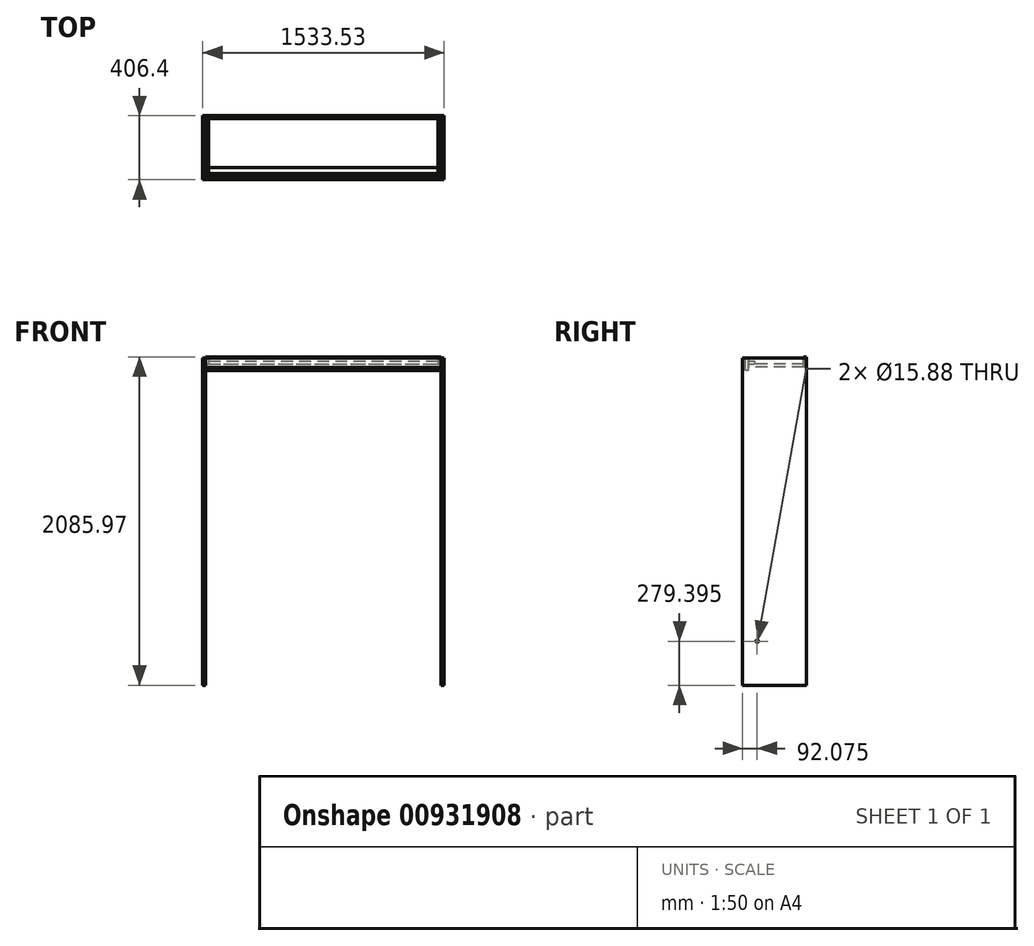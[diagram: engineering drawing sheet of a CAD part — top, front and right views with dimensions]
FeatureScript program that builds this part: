
annotation { "Feature Type Name" : "Feature", "Feature Type Description" : "" }
export const myFeature = defineFeature(function(context is Context, id is Id, definition is map)
    precondition{}
    {
        {
            var Q0;
            Q0=qCreatedBy(makeId("Top.planeOp"),FACE);
            var sketch = newSketch(context, id + "F0", { "sketchPlane" : qUnion([Q0])});
            skLineSegment(sketch, "E0.bottom", {"start": v(0, 0) * mm, "end": v(1495.43, 0) * mm});
            skLineSegment(sketch, "E0.top", {"start": v(0, -349.25) * mm, "end": v(1495.43, -349.25) * mm});
            skLineSegment(sketch, "E0.left", {"start": v(0, 0) * mm, "end": v(0, -349.25) * mm});
            skLineSegment(sketch, "E0.right", {"start": v(1495.43, 0) * mm, "end": v(1495.43, -349.25) * mm});
            skSolve(sketch);
        }
        {
            var Q0;
            Q0=makeQuery(id+"F0.imprint","IMPRINT",FACE,{"disambiguationData":[TD([[makeQuery(id+"F0.imprint","IMPRINT",EDGE,{"derivedFrom":sQuery(id+"F0.wireOp",EDGE,"E0.bottom")}),-1.0]])]});
            extrude(context, id + "F1", {"entities" : qUnion([Q0]), "depth" : 19.05 * mm, "offsetDistance" : 25.4 * mm});
        }
        {
            var Q0;
            Q0=makeQuery(id+"F1.opExtrude","CAP_FACE",FACE,{"disambiguationData":[OSD([sQuery(id+"F0.wireOp",EDGE,"E0.bottom"),sQuery(id+"F0.wireOp",EDGE,"E0.top"),sQuery(id+"F0.wireOp",EDGE,"E0.left"),sQuery(id+"F0.wireOp",EDGE,"E0.right")])],"isStart":false});
            var sketch = newSketch(context, id + "F2", { "sketchPlane" : qUnion([Q0])});
            skLineSegment(sketch, "E1.bottom", {"start": v(0, 0) * mm, "end": v(19.05, 0) * mm});
            skLineSegment(sketch, "E1.top", {"start": v(0, -349.25) * mm, "end": v(19.05, -349.25) * mm});
            skLineSegment(sketch, "E1.left", {"start": v(0, 0) * mm, "end": v(0, -349.25) * mm});
            skLineSegment(sketch, "E1.right", {"start": v(19.05, 0) * mm, "end": v(19.05, -349.25) * mm});
            skLineSegment(sketch, "E2.bottom", {"start": v(1495.43, 0) * mm, "end": v(1476.38, 0) * mm});
            skLineSegment(sketch, "E2.top", {"start": v(1495.43, -349.25) * mm, "end": v(1476.38, -349.25) * mm});
            skLineSegment(sketch, "E2.left", {"start": v(1495.43, 0) * mm, "end": v(1495.43, -349.25) * mm});
            skLineSegment(sketch, "E2.right", {"start": v(1476.38, 0) * mm, "end": v(1476.38, -349.25) * mm});
            skSolve(sketch);
        }
        {
            var Q0;
            Q0=makeQuery(id+"F2.imprint","IMPRINT",FACE,{"disambiguationData":[TD([[makeQuery(id+"F2.imprint","IMPRINT",EDGE,{"derivedFrom":sQuery(id+"F2.wireOp",EDGE,"E1.bottom")}),-1.0]])]});
            var Q1;
            Q1=makeQuery(id+"F2.imprint","IMPRINT",FACE,{"disambiguationData":[TD([[makeQuery(id+"F2.imprint","IMPRINT",EDGE,{"derivedFrom":sQuery(id+"F2.wireOp",EDGE,"E2.bottom")}),-1.0]])]});
            extrude(context, id + "F3", {"entities" : qUnion([Q0, Q1]), "depth" : 38.1 * mm, "offsetDistance" : 25.4 * mm});
        }
        {
            var Q0;
            Q0=qCreatedBy(makeId("Front.planeOp"),FACE);
            var sketch = newSketch(context, id + "F4", { "sketchPlane" : qUnion([Q0])});
            skLineSegment(sketch, "E3.bottom", {"start": v(1495.43, 0) * mm, "end": v(0, 0) * mm});
            skLineSegment(sketch, "E3.top", {"start": v(1495.43, 63.5) * mm, "end": v(0, 63.5) * mm});
            skLineSegment(sketch, "E3.left", {"start": v(1495.43, 0) * mm, "end": v(1495.43, 63.5) * mm});
            skLineSegment(sketch, "E3.right", {"start": v(0, 0) * mm, "end": v(0, 63.5) * mm});
            skSolve(sketch);
        }
        {
            var Q0;
            Q0=makeQuery(id+"F4.imprint","IMPRINT",FACE,{"disambiguationData":[TD([[makeQuery(id+"F4.imprint","IMPRINT",EDGE,{"derivedFrom":sQuery(id+"F4.wireOp",EDGE,"E3.bottom")}),-1.0]])]});
            extrude(context, id + "F5", {"entities" : qUnion([Q0]), "oppositeDirection" : true, "depth" : 19.05 * mm, "offsetDistance" : 25.4 * mm});
        }
        {
            var Q0;
            Q0=makeQuery(id+"F3.opExtrude","CAP_FACE",FACE,{"disambiguationData":[OSD([sQuery(id+"F2.wireOp",EDGE,"E1.bottom"),sQuery(id+"F2.wireOp",EDGE,"E1.top"),sQuery(id+"F2.wireOp",EDGE,"E1.left"),sQuery(id+"F2.wireOp",EDGE,"E1.right")])],"isStart":false});
            var sketch = newSketch(context, id + "F6", { "sketchPlane" : qUnion([Q0])});
            skLineSegment(sketch, "E4.bottom", {"start": v(0, -349.25) * mm, "end": v(1495.43, -349.25) * mm});
            skLineSegment(sketch, "E4.top", {"start": v(0, -368.3) * mm, "end": v(1495.43, -368.3) * mm});
            skLineSegment(sketch, "E4.left", {"start": v(0, -349.25) * mm, "end": v(0, -368.3) * mm});
            skLineSegment(sketch, "E4.right", {"start": v(1495.43, -349.25) * mm, "end": v(1495.43, -368.3) * mm});
            skLineSegment(sketch, "E5", {"start": v(0, -368.3) * mm, "end": v(0, -387.35) * mm});
            skLineSegment(sketch, "E6", {"start": v(0, -387.35) * mm, "end": v(1495.43, -387.35) * mm});
            skLineSegment(sketch, "E7", {"start": v(1495.43, -387.35) * mm, "end": v(1495.43, -368.3) * mm});
            skLineSegment(sketch, "E8.bottom", {"start": v(0, 19.05) * mm, "end": v(-19.05, 19.05) * mm});
            skLineSegment(sketch, "E8.top", {"start": v(0, -387.35) * mm, "end": v(-19.05, -387.35) * mm});
            skLineSegment(sketch, "E8.left", {"start": v(0, 19.05) * mm, "end": v(0, -387.35) * mm});
            skLineSegment(sketch, "E8.right", {"start": v(-19.05, 19.05) * mm, "end": v(-19.05, -387.35) * mm});
            skLineSegment(sketch, "E9.bottom", {"start": v(1495.43, 19.05) * mm, "end": v(1514.48, 19.05) * mm});
            skLineSegment(sketch, "E9.top", {"start": v(1495.43, -387.35) * mm, "end": v(1514.48, -387.35) * mm});
            skLineSegment(sketch, "E9.left", {"start": v(1495.43, 19.05) * mm, "end": v(1495.43, -387.35) * mm});
            skLineSegment(sketch, "E9.right", {"start": v(1514.48, 19.05) * mm, "end": v(1514.48, -387.35) * mm});
            skSolve(sketch);
        }
        {
            var Q0;
            Q0=makeQuery(id+"F6.imprint","IMPRINT",FACE,{"disambiguationData":[TD([[makeQuery(id+"F6.imprint","IMPRINT",EDGE,{"derivedFrom":sQuery(id+"F6.wireOp",EDGE,"E4.top")}),1.0]])]});
            extrude(context, id + "F7", {"entities" : qUnion([Q0]), "oppositeDirection" : true, "depth" : 79.38 * mm, "offsetDistance" : 25.4 * mm});
        }
        {
            var Q0;
            Q0=makeQuery(id+"F6.imprint","IMPRINT",FACE,{"disambiguationData":[TD([[makeQuery(id+"F6.imprint","IMPRINT",EDGE,{"derivedFrom":sQuery(id+"F6.wireOp",EDGE,"E4.top")}),-1.0]])]});
            extrude(context, id + "F8", {"entities" : qUnion([Q0]), "oppositeDirection" : true, "depth" : 60.32 * mm, "offsetDistance" : 25.4 * mm});
        }
        {
            var Q0;
            Q0=makeQuery(id+"F1.opExtrude","CAP_FACE",FACE,{"disambiguationData":[OSD([sQuery(id+"F0.wireOp",EDGE,"E0.bottom"),sQuery(id+"F0.wireOp",EDGE,"E0.top"),sQuery(id+"F0.wireOp",EDGE,"E0.left"),sQuery(id+"F0.wireOp",EDGE,"E0.right")])],"isStart":false});
            var sketch = newSketch(context, id + "F9", { "sketchPlane" : qUnion([Q0])});
            skLineSegment(sketch, "E10.bottom", {"start": v(1476.38, -349.25) * mm, "end": v(19.05, -349.25) * mm});
            skLineSegment(sketch, "E10.top", {"start": v(1476.38, -311.15) * mm, "end": v(19.05, -311.15) * mm});
            skLineSegment(sketch, "E10.left", {"start": v(1476.38, -349.25) * mm, "end": v(1476.38, -311.15) * mm});
            skLineSegment(sketch, "E10.right", {"start": v(19.05, -349.25) * mm, "end": v(19.05, -311.15) * mm});
            skSolve(sketch);
        }
        {
            var Q0;
            Q0=makeQuery(id+"F9.imprint","IMPRINT",FACE,{"disambiguationData":[TD([[makeQuery(id+"F9.imprint","IMPRINT",EDGE,{"derivedFrom":sQuery(id+"F9.wireOp",EDGE,"E10.bottom")}),1.0]])]});
            extrude(context, id + "F10", {"entities" : qUnion([Q0]), "depth" : 19.05 * mm, "offsetDistance" : 25.4 * mm});
        }
        {
            var Q0;
            {var subQ1=sQuery(id+"F6.wireOp",EDGE,"E4.left");Q0=makeQuery(id+"F6.imprint","IMPRINT",FACE,{"disambiguationData":[TD([[makeQuery(id+"F6.imprint","IMPRINT",EDGE,{"derivedFrom":subQ1}),-1.0]])]});}
            var Q1;
            Q1=makeQuery(id+"F6.imprint","IMPRINT",FACE,{"disambiguationData":[TD([[makeQuery(id+"F6.imprint","IMPRINT",EDGE,{"derivedFrom":sQuery(id+"F6.wireOp",EDGE,"E4.right")}),1.0]])]});
            extrude(context, id + "F11", {"entities" : qUnion([Q0, Q1]), "oppositeDirection" : true, "depth" : 2079.62 * mm, "offsetDistance" : 25.4 * mm});
        }
        {
            var Q0;
            Q0=makeQuery(id+"F11.opExtrude","SWEPT_FACE",FACE,{"disambiguationData":[OSD([sQuery(id+"F6.wireOp",EDGE,"E4.left"),sQuery(id+"F6.wireOp",EDGE,"E5"),sQuery(id+"F6.wireOp",EDGE,"E8.left")])]});
            var sketch = newSketch(context, id + "F12", { "sketchPlane" : qUnion([Q0])});
            skCircle(sketch, "E11", {"center": v(-295.28, -1743.07) * mm, "radius": 7.94 * mm});
            skSolve(sketch);
        }
        {
            var Q0;
            Q0 = qSketchRegion(id + "F12", true);
            extrude(context, id + "F13", {"entities" : qUnion([Q0]), "operationType" : NewBodyOperationType.REMOVE, "endBound" : BoundingType.THROUGH_ALL, "oppositeDirection" : true, "depth" : 25.4 * mm, "offsetDistance" : 25.4 * mm, "hasSecondDirection" : true, "secondDirectionBound" : BoundingType.THROUGH_ALL, "secondDirectionOppositeDirection" : false, "secondDirectionDepth" : 25.4 * mm});
        }
    });
